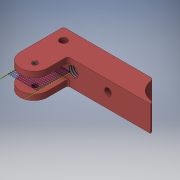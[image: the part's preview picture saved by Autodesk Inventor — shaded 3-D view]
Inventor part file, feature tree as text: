
AUTODESK INVENTOR PART (.ipt)
format: ipt  version: 2016 SP1 (Build 200210100, 210)  size: 265,728 bytes
history: native  units: in
note: dims shown in document units (in); Inventor stores cm internally (conversion verified against a paired STEP export)
features: sketch x7, other x3
ambient origin geometry x8: Origin, YZ Plane, XZ Plane, XY Plane, X Axis, Y Axis, Z Axis, Center Point
bodies: Solid1 (feature_tree)
feature tree (10):
  other  "Part2.ipt"
  other  "Solid1::Part2.ipt"
  other  "TaggingFeature1"
  sketch  "Sketch1"  dims[d0=0.3937in]
  sketch  "Sketch2"
  sketch  "Sketch3"
  sketch  "Sketch4"
  sketch  "Sketch5"
  sketch  "Sketch6"
  sketch  "Sketch7"
